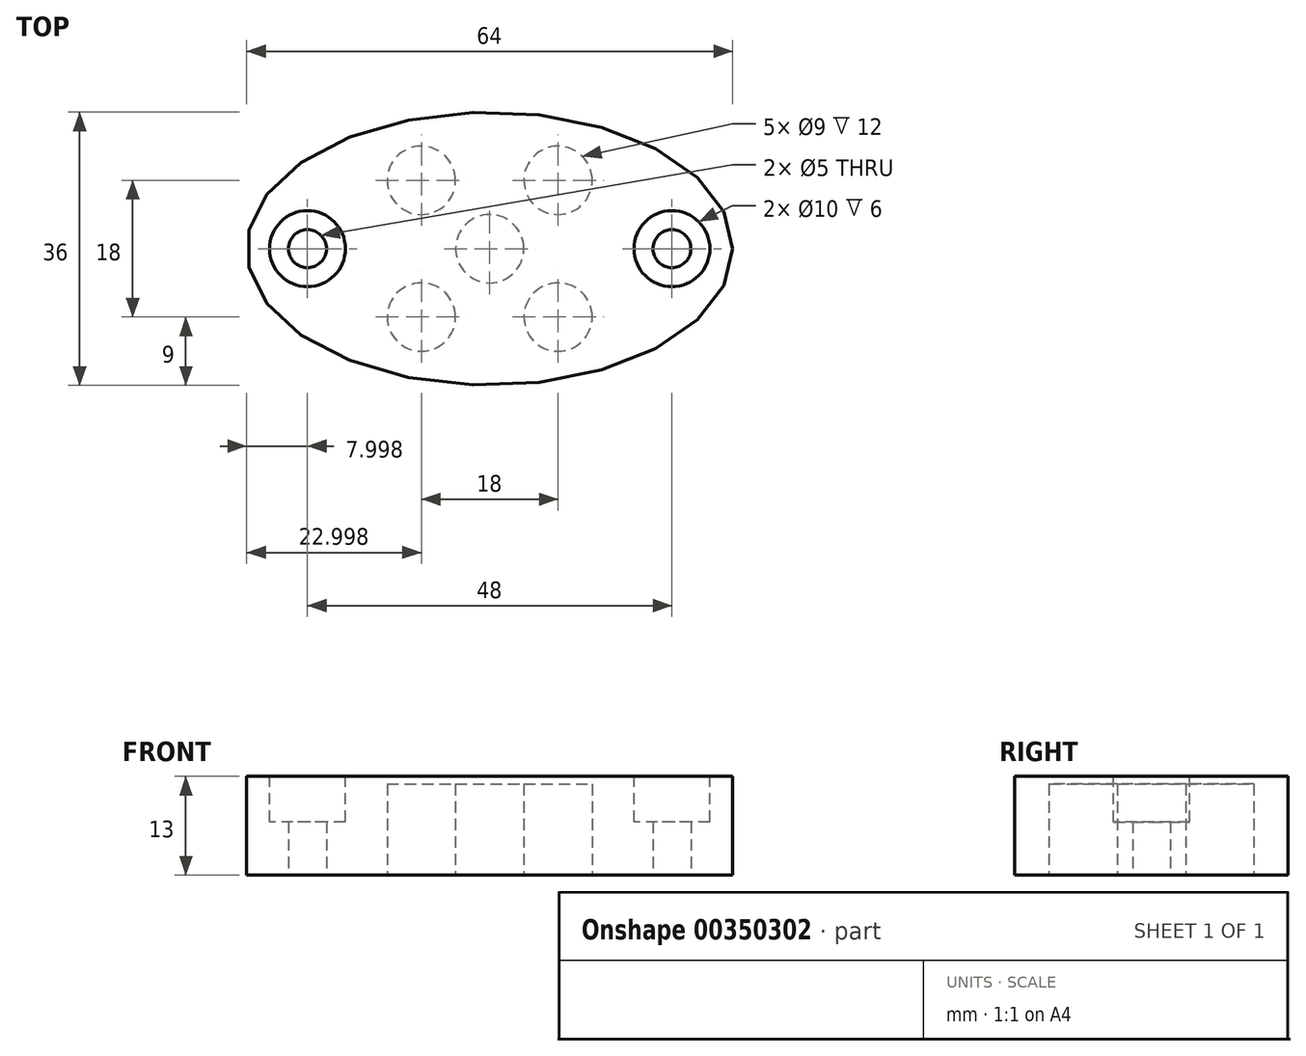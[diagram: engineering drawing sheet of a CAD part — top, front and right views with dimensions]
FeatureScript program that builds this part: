
annotation { "Feature Type Name" : "Feature", "Feature Type Description" : "" }
export const myFeature = defineFeature(function(context is Context, id is Id, definition is map)
    precondition{}
    {
        {
            var Q0;
            Q0=qCreatedBy(makeId("Top.planeOp"),FACE);
            var sketch = newSketch(context, id + "F0", { "sketchPlane" : qUnion([Q0])});
            skEllipse(sketch, "E0", {"center": v(-27.82, 0) * mm, "majorRadius": 32 * mm, "minorRadius": 18 * mm, "majorAxis": v(1, 0)});
            skLineSegment(sketch, "E1", {"start": v(-59.82, 0) * mm, "end": v(4.18, 0) * mm, "construction": true});
            skPoint(sketch, "E2", {"position": v(-51.82, 0) * mm});
            skPoint(sketch, "E3", {"position": v(-3.82, 0) * mm});
            skCircle(sketch, "E4", {"center": v(-51.82, 0) * mm, "radius": 2.5 * mm});
            skCircle(sketch, "E5", {"center": v(-3.82, 0) * mm, "radius": 2.5 * mm});
            skSolve(sketch);
        }
        {
            var Q0;
            Q0 = qSketchRegion(id + "F0", true);
            extrude(context, id + "F1", {"entities" : qUnion([Q0]), "depth" : 13 * mm});
        }
        {
            var Q0;
            Q0=makeQuery(id+"F1.opExtrude","CAP_FACE",FACE,{"disambiguationData":[OSD([sQuery(id+"F0.wireOp",EDGE,"E0"),sQuery(id+"F0.wireOp",EDGE,"E4"),sQuery(id+"F0.wireOp",EDGE,"E5")])],"isStart":false});
            var sketch = newSketch(context, id + "F2", { "sketchPlane" : qUnion([Q0])});
            skCircle(sketch, "E6", {"center": v(-51.82, 0) * mm, "radius": 5 * mm});
            skCircle(sketch, "E7", {"center": v(-3.82, 0) * mm, "radius": 5 * mm});
            skSolve(sketch);
        }
        {
            var Q0;
            Q0 = qSketchRegion(id + "F2", true);
            extrude(context, id + "F3", {"entities" : qUnion([Q0]), "operationType" : NewBodyOperationType.REMOVE, "oppositeDirection" : true, "depth" : 6 * mm});
        }
        {
            var Q0;
            Q0=makeQuery(id+"F1.opExtrude","CAP_FACE",FACE,{"disambiguationData":[OSD([sQuery(id+"F0.wireOp",EDGE,"E0"),sQuery(id+"F0.wireOp",EDGE,"E4"),sQuery(id+"F0.wireOp",EDGE,"E5")])],"isStart":true});
            var sketch = newSketch(context, id + "F4", { "sketchPlane" : qUnion([Q0])});
            skLineSegment(sketch, "E8.bottom", {"start": v(-18.82, -9) * mm, "end": v(-36.82, -9) * mm, "construction": true});
            skLineSegment(sketch, "E8.top", {"start": v(-18.82, 9) * mm, "end": v(-36.82, 9) * mm, "construction": true});
            skLineSegment(sketch, "E8.left", {"start": v(-18.82, -9) * mm, "end": v(-18.82, 9) * mm, "construction": true});
            skLineSegment(sketch, "E8.right", {"start": v(-36.82, -9) * mm, "end": v(-36.82, 9) * mm, "construction": true});
            skPoint(sketch, "E8.middle", {"position": v(-27.82, 0) * mm});
            skCircle(sketch, "E9", {"center": v(-36.82, 9) * mm, "radius": 4.5 * mm});
            skCircle(sketch, "E10", {"center": v(-18.82, 9) * mm, "radius": 4.5 * mm});
            skCircle(sketch, "E11", {"center": v(-36.82, -9) * mm, "radius": 4.5 * mm});
            skCircle(sketch, "E12", {"center": v(-18.82, -9) * mm, "radius": 4.5 * mm});
            skCircle(sketch, "E13", {"center": v(-27.82, 0) * mm, "radius": 4.5 * mm});
            skSolve(sketch);
        }
        {
            var Q0;
            Q0 = qSketchRegion(id + "F4", true);
            extrude(context, id + "F5", {"entities" : qUnion([Q0]), "operationType" : NewBodyOperationType.REMOVE, "oppositeDirection" : true, "depth" : 12 * mm});
        }
    });
